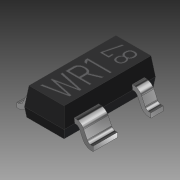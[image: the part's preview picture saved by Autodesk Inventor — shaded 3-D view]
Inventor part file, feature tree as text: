
AUTODESK INVENTOR PART (.ipt)
format: ipt  version: 2016 (Build 200138000, 138)  size: 329,728 bytes
history: native  units: mm
features: chamfer x8, sketch x5, plane x3, extrude x2, sweep x2, projected_geometry x2
ambient origin geometry x8: Origin, YZ Plane, XZ Plane, XY Plane, X Axis, Y Axis, Z Axis, Center Point
bodies: Body1 (feature_tree)
feature tree (22):
  extrude  "Extrusion4"  Depth=0.3mm
  chamfer  "Chamfer1"  Distance=3.0mm
  chamfer  "Chamfer3"  Distance=0.6mm
  chamfer  "Chamfer4"  Distance=0.3mm
  chamfer  "Chamfer5"  Distance=2.0mm
  chamfer  "Chamfer2"  Distance=2.0mm
  chamfer  "Chamfer6"  Distance=2.0mm
  chamfer  "Chamfer7"  Distance=2.0mm
  chamfer  "Chamfer8"  Distance=0.3mm
  extrude  "Extrusion5"  Depth=0.15mm
  plane  "Work Plane1"
  sketch  "Sketch11"  dims[d17=0.6mm d18=2.0mm d19=1.22173mm]
  plane  "Work Plane2"
  sketch  "Sketch12"  dims[d20=0.6mm d21=2.0mm d22=1.22173mm]
  plane  "Work Plane3"
  sweep  "Sweep2"
  sweep  "Sweep1"
  sketch  "Sketch10"  dims[d7=0.9mm d8=1.3mm d9=3.0mm d10=0.0mm d11=0.6mm d12=2.0mm d13=1.22173mm d14=0.3mm d15=2.0mm d16=1.22173mm]
  projected_geometry  "Projected Loop1"
  sketch  "Sketch13"  dims[d23=0.6mm d24=2.0mm d25=1.22173mm]
  sketch  "Sketch14"  dims[d26=0.3mm d27=2.0mm d28=1.22173mm d29=0.3mm d30=2.0mm d31=1.22173mm d32=0.3mm d33=2.0mm d34=1.22173mm d35=90.0deg d37=0.8mm d38=0.4mm d39=0.15mm d40=2.3mm d41=90.0deg d42=1.25mm d43=1.025mm d45=0.225mm d46=0.2mm d47=11.34464mm d48=0.0mm d49=0.0mm d50=90.0deg d51=0.0mm d52=0.0mm d53=0.25mm d54=1.5mm d55=1.0mm d56=0.6mm d57=0.15mm d58=0.01mm d59=0.0mm]
  projected_geometry  "Projected Loop2"
